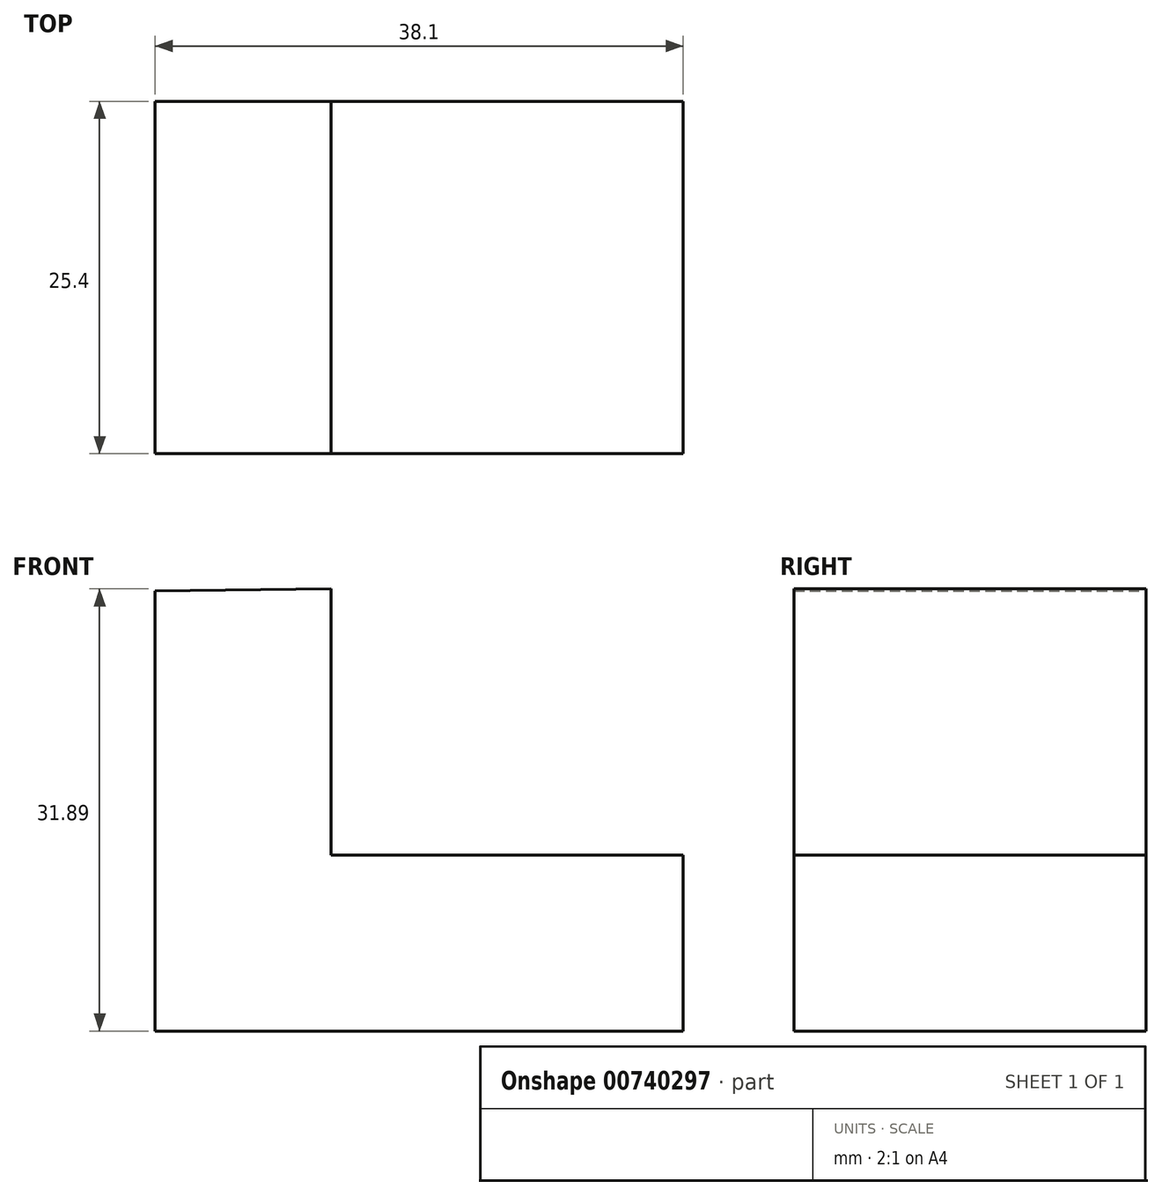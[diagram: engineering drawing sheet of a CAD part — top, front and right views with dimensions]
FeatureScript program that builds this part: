
annotation { "Feature Type Name" : "Feature", "Feature Type Description" : "" }
export const myFeature = defineFeature(function(context is Context, id is Id, definition is map)
    precondition{}
    {
        {
            var Q0;
            Q0=qCreatedBy(makeId("Front.planeOp"),FACE);
            var sketch = newSketch(context, id + "F0", { "sketchPlane" : qUnion([Q0])});
            skLineSegment(sketch, "E0", {"start": v(0, 31.75) * mm, "end": v(0, 0) * mm});
            skLineSegment(sketch, "E1", {"start": v(0, 0) * mm, "end": v(38.1, 0) * mm});
            skLineSegment(sketch, "E2", {"start": v(38.1, 0) * mm, "end": v(38.1, 12.7) * mm});
            skLineSegment(sketch, "E3", {"start": v(38.1, 12.7) * mm, "end": v(12.7, 12.7) * mm});
            skLineSegment(sketch, "E4", {"start": v(12.7, 12.7) * mm, "end": v(12.7, 31.89) * mm});
            skLineSegment(sketch, "E5", {"start": v(12.7, 31.89) * mm, "end": v(0, 31.75) * mm});
            skSolve(sketch);
        }
        {
            var Q0;
            Q0 = qSketchRegion(id + "F0", true);
            extrude(context, id + "F1", {"entities" : qUnion([Q0]), "depth" : 25.4 * mm, "offsetDistance" : 25.4 * mm});
        }
    });
